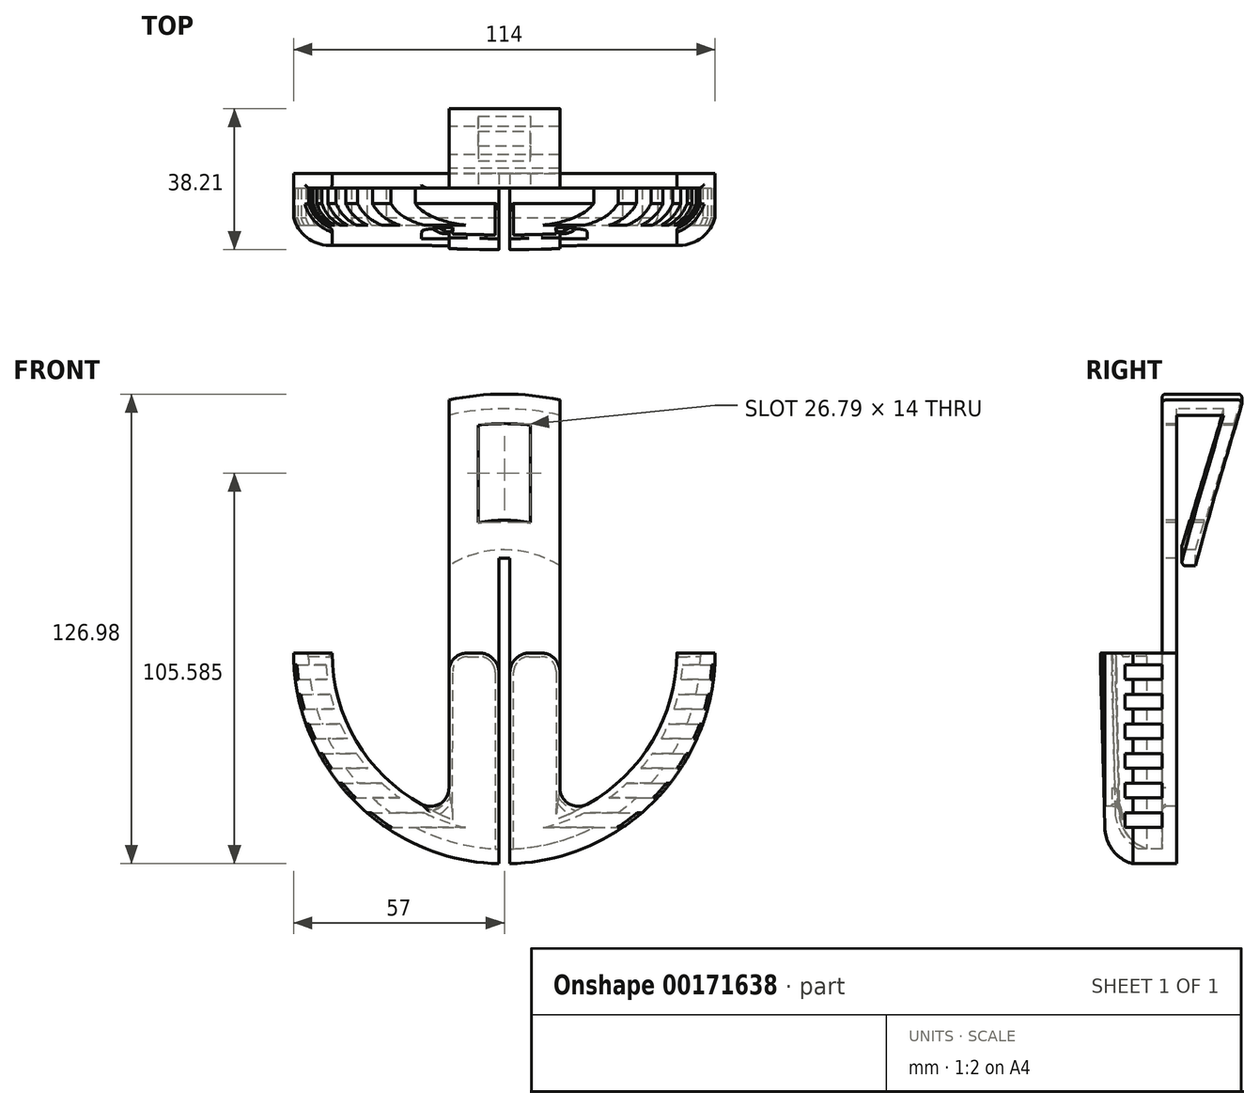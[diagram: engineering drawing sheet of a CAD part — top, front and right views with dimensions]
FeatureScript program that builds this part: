
annotation { "Feature Type Name" : "Feature", "Feature Type Description" : "" }
export const myFeature = defineFeature(function(context is Context, id is Id, definition is map)
    precondition{}
    {
        {
            var Q0;
            Q0=qCreatedBy(makeId("Top.planeOp"),FACE);
            var sketch = newSketch(context, id + "F0", { "sketchPlane" : qUnion([Q0])});
            skLineSegment(sketch, "E0", {"start": v(0, 0) * mm, "end": v(53, 0) * mm});
            skLineSegment(sketch, "E1", {"start": v(53, 0) * mm, "end": v(53, -4.13) * mm});
            skArc(sketch, "E2", {"start": v(42.97, -11.58) * mm, "mid": v(49.16, -9.44) * mm, "end": v(53, -4.13) * mm});
            skLineSegment(sketch, "E3", {"start": v(57, 4) * mm, "end": v(57, -7.88) * mm});
            skArc(sketch, "E4", {"start": v(47.4, -15.46) * mm, "mid": v(53.45, -13.27) * mm, "end": v(57, -7.88) * mm});
            skLineSegment(sketch, "E5", {"start": v(42.97, -11.58) * mm, "end": v(3.35, -12.64) * mm});
            skLineSegment(sketch, "E6", {"start": v(3.35, -12.64) * mm, "end": v(3.35, -16.64) * mm});
            skLineSegment(sketch, "E7", {"start": v(3.35, -16.64) * mm, "end": v(47.4, -15.46) * mm});
            skLineSegment(sketch, "E8", {"start": v(0, 4) * mm, "end": v(57, 4) * mm});
            skLineSegment(sketch, "E9", {"start": v(0, 4) * mm, "end": v(0, 0) * mm});
            skSolve(sketch);
        }
        {
            var Q0;
            Q0=makeQuery(id+"F0.imprint","IMPRINT",FACE,{"disambiguationData":[TD([[makeQuery(id+"F0.imprint","IMPRINT",EDGE,{"derivedFrom":sQuery(id+"F0.wireOp",EDGE,"E0")}),1.0]])]});
            var Q1;
            Q1=sQuery(id+"F0.wireOp",EDGE,"gh6nvR1q-v7TM-2IOc-XlZp-swlE0I2HpCQy");
            var Q2;
            Q2=sQuery(id+"F0.wireOp",EDGE,"O8IQiqjr-gjum-d30m-pnRi-cYj8KfRXyHnp");
            var Q3;
            Q3=sQuery(id+"F0.wireOp",EDGE,"gTedTpXi-uLA1-ukL2-yQAW-aUygu7Kv1SXh");
            var Q4;
            Q4=sQuery(id+"F0.wireOp",EDGE,"ZykMHYlj-tlNZ-H5aW-ebbf-Yw6o6fal1dPa");
            var Q5;
            Q5=sQuery(id+"F0.wireOp",EDGE,"cCRbS5nW-RNkD-MFLE-ALEK-Vklt7AKWVduu");
            var Q6;
            Q6=sQuery(id+"F0.wireOp",EDGE,"nLixHNUd-pwQR-5I1a-BRTQ-ecuvHCXoE5qB");
            var Q7;
            Q7=sQuery(id+"F0.wireOp",EDGE,"kgJvfNm7-WcT3-KGPc-acBb-M34wcv6vBjd2");
            var Q8;
            Q8=sQuery(id+"F0.wireOp",EDGE,"E5");
            var Q9;
            Q9=sQuery(id+"F0.wireOp",EDGE,"E2");
            var Q10;
            Q10=sQuery(id+"F0.wireOp",EDGE,"E4");
            var Q11;
            Q11=sQuery(id+"F0.wireOp",EDGE,"E7");
            var Q12;
            Q12=sQuery(id+"F0.wireOp",EDGE,"E3");
            var Q13;
            Q13=sQuery(id+"F0.wireOp",EDGE,"E1");
            var Q14;
            Q14=sQuery(id+"F0.wireOp",EDGE,"E6");
            var Q15;
            Q15=sQuery(id+"F0.wireOp",EDGE,"E9");
            revolve(context, id + "F1", {"entities" : qUnion([Q0]), "surfaceEntities" : qUnion([Q1, Q2, Q3, Q4, Q5, Q6, Q7, Q8, Q9, Q10, Q11, Q12, Q13, Q14]), "axis" : qUnion([Q15]), "revolveType" : RevolveType.ONE_DIRECTION, "oppositeDirection" : true, "angle" : 180 * degree});
        }
        {
            var Q0;
            Q0=qCreatedBy(makeId("Top.planeOp"),FACE);
            var sketch = newSketch(context, id + "F2", { "sketchPlane" : qUnion([Q0])});
            skLineSegment(sketch, "E10", {"start": v(0, 0) * mm, "end": v(-70, 0) * mm});
            skLineSegment(sketch, "E11", {"start": v(-70, 0) * mm, "end": v(-70, 21.93) * mm});
            skLineSegment(sketch, "E12", {"start": v(-70, 21.93) * mm, "end": v(-27.9, 9.03) * mm});
            skLineSegment(sketch, "E13", {"start": v(-27.9, 9.03) * mm, "end": v(-27.9, 5.03) * mm});
            skLineSegment(sketch, "E14", {"start": v(-27.9, 5.03) * mm, "end": v(-66, 16.7) * mm});
            skLineSegment(sketch, "E15", {"start": v(-66, 16.7) * mm, "end": v(-66, 4) * mm});
            skLineSegment(sketch, "E16", {"start": v(-66, 4) * mm, "end": v(0, 4) * mm});
            skLineSegment(sketch, "E17", {"start": v(0, 4) * mm, "end": v(0, 0) * mm});
            skSolve(sketch);
        }
        {
            var Q0;
            Q0=makeQuery(id+"F2.imprint","IMPRINT",FACE,{"disambiguationData":[TD([[makeQuery(id+"F2.imprint","IMPRINT",EDGE,{"derivedFrom":sQuery(id+"F2.wireOp",EDGE,"E10")}),-1.0]])]});
            var Q1;
            Q1=sQuery(id+"F2.wireOp",EDGE,"E17");
            revolve(context, id + "F3", {"operationType" : NewBodyOperationType.ADD, "entities" : qUnion([Q0]), "axis" : qUnion([Q1]), "revolveType" : RevolveType.ONE_DIRECTION, "oppositeDirection" : true, "angle" : 180 * degree});
        }
        {
            var Q0;
            Q0=qCreatedBy(makeId("Front.planeOp"),FACE);
            var sketch = newSketch(context, id + "F4", { "sketchPlane" : qUnion([Q0])});
            skLineSegment(sketch, "E18", {"start": v(-15, 0) * mm, "end": v(-15, 77.6) * mm});
            skLineSegment(sketch, "E19", {"start": v(-15, 77.6) * mm, "end": v(-78.11, 77.6) * mm});
            skLineSegment(sketch, "E20", {"start": v(-78.11, 77.6) * mm, "end": v(-78.11, 0) * mm});
            skLineSegment(sketch, "E21", {"start": v(-78.11, 0) * mm, "end": v(-46.6, 0) * mm});
            skLineSegment(sketch, "E22", {"start": v(-15, 0) * mm, "end": v(-15, -44.13) * mm});
            skArc(sketch, "E23", {"start": v(-46.6, 0) * mm, "mid": v(-37.89, -27.14) * mm, "end": v(-15, -44.13) * mm});
            skLineSegment(sketch, "E24.MirrorCS", {"start": v(15, 0) * mm, "end": v(15, 77.6) * mm});
            skLineSegment(sketch, "E25.MirrorCS", {"start": v(15, 77.6) * mm, "end": v(78.11, 77.6) * mm});
            skLineSegment(sketch, "E26.MirrorCS", {"start": v(78.11, 77.6) * mm, "end": v(78.11, 0) * mm});
            skLineSegment(sketch, "E27.MirrorCS", {"start": v(78.11, 0) * mm, "end": v(46.6, 0) * mm});
            skArc(sketch, "E28.MirrorCS", {"start": v(46.6, 0) * mm, "mid": v(37.89, -27.14) * mm, "end": v(15, -44.13) * mm});
            skLineSegment(sketch, "E29.MirrorCS", {"start": v(15, 0) * mm, "end": v(15, -44.13) * mm});
            skLineSegment(sketch, "E30", {"start": v(0, 25.58) * mm, "end": v(1.5, 25.58) * mm});
            skLineSegment(sketch, "E31", {"start": v(1.5, 25.58) * mm, "end": v(1.5, -61.51) * mm});
            skLineSegment(sketch, "E32", {"start": v(1.5, -61.51) * mm, "end": v(-1.5, -61.51) * mm});
            skLineSegment(sketch, "E33", {"start": v(-1.5, -61.51) * mm, "end": v(-1.5, 25.58) * mm});
            skLineSegment(sketch, "E34", {"start": v(-1.5, 25.58) * mm, "end": v(0, 25.58) * mm});
            skArc(sketch, "E35", {"start": v(7, 35.21) * mm, "mid": v(0, 35.9) * mm, "end": v(-7, 35.21) * mm});
            skLineSegment(sketch, "E36", {"start": v(7, 35.21) * mm, "end": v(7, 61.6) * mm});
            skLineSegment(sketch, "E37", {"start": v(-7, 61.6) * mm, "end": v(-7, 35.21) * mm});
            skArc(sketch, "E38", {"start": v(7, 61.6) * mm, "mid": v(0, 62) * mm, "end": v(-7, 61.6) * mm});
            skSolve(sketch);
        }
        {
            var Q0;
            Q0 = qSketchRegion(id + "F4", true);
            extrude(context, id + "F5", {"entities" : qUnion([Q0]), "operationType" : NewBodyOperationType.REMOVE, "oppositeDirection" : true, "depth" : 25 * mm, "hasSecondDirection" : true, "secondDirectionOppositeDirection" : false, "secondDirectionDepth" : 49.3 * mm});
        }
        {
            var Q0;
            Q0=makeQuery(id+"F5.boolean.opBoolean","INTERSECT",EDGE,{"derivedFrom":[makeQuery(id+"F3.boolean.opBoolean","MERGE",FACE,{"derivedFrom":[makeQuery(id+"F1.opRevolve","SWEPT_FACE",FACE,{"disambiguationData":[OSD([sQuery(id+"F0.wireOp",EDGE,"E0")])]}),makeQuery(id+"F3.opRevolve","SWEPT_FACE",FACE,{"disambiguationData":[OSD([sQuery(id+"F2.wireOp",EDGE,"E10")])]})]}),makeQuery(id+"F5.opExtrude","SWEPT_FACE",FACE,{"disambiguationData":[OSD([sQuery(id+"F4.wireOp",EDGE,"E23")])]})]});
            var Q1;
            Q1=makeQuery(id+"F5.boolean.opBoolean","INTERSECT",EDGE,{"derivedFrom":[makeQuery(id+"F3.boolean.opBoolean","MERGE",FACE,{"derivedFrom":[makeQuery(id+"F1.opRevolve","SWEPT_FACE",FACE,{"disambiguationData":[OSD([sQuery(id+"F0.wireOp",EDGE,"E0")])]}),makeQuery(id+"F3.opRevolve","SWEPT_FACE",FACE,{"disambiguationData":[OSD([sQuery(id+"F2.wireOp",EDGE,"E10")])]})]}),makeQuery(id+"F5.opExtrude","SWEPT_FACE",FACE,{"disambiguationData":[OSD([sQuery(id+"F4.wireOp",EDGE,"E21")])]})]});
            var Q2;
            Q2=makeQuery(id+"F1.opRevolve","CAP_EDGE",EDGE,{"disambiguationData":[OSD([sQuery(id+"F0.wireOp",EDGE,"E1")])],"isStart":false});
            var Q3;
            Q3=makeQuery(id+"F1.opRevolve","CAP_EDGE",EDGE,{"disambiguationData":[OSD([sQuery(id+"F0.wireOp",EDGE,"E2")])],"isStart":false});
            var Q4;
            Q4=makeQuery(id+"F5.boolean.opBoolean","INTERSECT",EDGE,{"derivedFrom":[makeQuery(id+"F1.opRevolve","SWEPT_FACE",FACE,{"disambiguationData":[OSD([sQuery(id+"F0.wireOp",EDGE,"E2")])]}),makeQuery(id+"F5.opExtrude","SWEPT_FACE",FACE,{"disambiguationData":[OSD([sQuery(id+"F4.wireOp",EDGE,"E23")])]})]});
            var Q5;
            Q5=makeQuery(id+"F5.boolean.opBoolean","INTERSECT",EDGE,{"derivedFrom":[makeQuery(id+"F1.opRevolve","SWEPT_FACE",FACE,{"disambiguationData":[OSD([sQuery(id+"F0.wireOp",EDGE,"E2")])]}),makeQuery(id+"F5.opExtrude","SWEPT_FACE",FACE,{"disambiguationData":[OSD([sQuery(id+"F4.wireOp",EDGE,"E18"),sQuery(id+"F4.wireOp",EDGE,"E22")])]})]});
            var Q6;
            Q6=makeQuery(id+"F5.boolean.opBoolean","INTERSECT",EDGE,{"derivedFrom":[makeQuery(id+"F1.opRevolve","SWEPT_FACE",FACE,{"disambiguationData":[OSD([sQuery(id+"F0.wireOp",EDGE,"E5")])]}),makeQuery(id+"F5.opExtrude","SWEPT_FACE",FACE,{"disambiguationData":[OSD([sQuery(id+"F4.wireOp",EDGE,"E18"),sQuery(id+"F4.wireOp",EDGE,"E22")])]})]});
            var Q7;
            Q7=makeQuery(id+"F1.opRevolve","CAP_EDGE",EDGE,{"disambiguationData":[OSD([sQuery(id+"F0.wireOp",EDGE,"E5")])],"isStart":false});
            var Q8;
            {var subQ0=sQuery(id+"F0.wireOp",EDGE,"E6");var subQ1=sQuery(id+"F0.wireOp",EDGE,"E5");Q8=makeQuery(id+"F5.boolean.opBoolean","SPLIT",EDGE,{"disambiguationData":[TD([makeQuery(id+"F5.opExtrude","SWEPT_FACE",FACE,{"disambiguationData":[OSD([sQuery(id+"F4.wireOp",EDGE,"E33")])]})])],"derivedFrom":makeQuery(id+"F1.opRevolve","SWEPT_EDGE",EDGE,{"disambiguationData":[OSD([subQ1,subQ0])]})});}
            var Q9;
            Q9=makeQuery(id+"F5.boolean.opBoolean","INTERSECT",EDGE,{"derivedFrom":[makeQuery(id+"F1.opRevolve","SWEPT_FACE",FACE,{"disambiguationData":[OSD([sQuery(id+"F0.wireOp",EDGE,"E5")])]}),makeQuery(id+"F5.opExtrude","SWEPT_FACE",FACE,{"disambiguationData":[OSD([sQuery(id+"F4.wireOp",EDGE,"E33")])]})]});
            var Q10;
            Q10=makeQuery(id+"F5.boolean.opBoolean","INTERSECT",EDGE,{"derivedFrom":[makeQuery(id+"F1.opRevolve","SWEPT_FACE",FACE,{"disambiguationData":[OSD([sQuery(id+"F0.wireOp",EDGE,"E2")])]}),makeQuery(id+"F5.opExtrude","SWEPT_FACE",FACE,{"disambiguationData":[OSD([sQuery(id+"F4.wireOp",EDGE,"E31")])]})]});
            var Q11;
            {var subQ0=sQuery(id+"F0.wireOp",EDGE,"E6");var subQ1=sQuery(id+"F0.wireOp",EDGE,"E5");Q11=makeQuery(id+"F5.boolean.opBoolean","SPLIT",EDGE,{"disambiguationData":[TD([makeQuery(id+"F5.opExtrude","SWEPT_FACE",FACE,{"disambiguationData":[OSD([sQuery(id+"F4.wireOp",EDGE,"E31")])]})])],"derivedFrom":makeQuery(id+"F1.opRevolve","SWEPT_EDGE",EDGE,{"disambiguationData":[OSD([subQ1,subQ0])]})});}
            var Q12;
            Q12=makeQuery(id+"F1.opRevolve","CAP_EDGE",EDGE,{"disambiguationData":[OSD([sQuery(id+"F0.wireOp",EDGE,"E5")])],"isStart":true});
            var Q13;
            Q13=makeQuery(id+"F5.boolean.opBoolean","INTERSECT",EDGE,{"derivedFrom":[makeQuery(id+"F1.opRevolve","SWEPT_FACE",FACE,{"disambiguationData":[OSD([sQuery(id+"F0.wireOp",EDGE,"E5")])]}),makeQuery(id+"F5.opExtrude","SWEPT_FACE",FACE,{"disambiguationData":[OSD([sQuery(id+"F4.wireOp",EDGE,"E24.MirrorCS"),sQuery(id+"F4.wireOp",EDGE,"E29.MirrorCS")])]})]});
            var Q14;
            Q14=makeQuery(id+"F5.boolean.opBoolean","INTERSECT",EDGE,{"derivedFrom":[makeQuery(id+"F1.opRevolve","SWEPT_FACE",FACE,{"disambiguationData":[OSD([sQuery(id+"F0.wireOp",EDGE,"E2")])]}),makeQuery(id+"F5.opExtrude","SWEPT_FACE",FACE,{"disambiguationData":[OSD([sQuery(id+"F4.wireOp",EDGE,"E28.MirrorCS")])]})]});
            var Q15;
            Q15=makeQuery(id+"F1.opRevolve","CAP_EDGE",EDGE,{"disambiguationData":[OSD([sQuery(id+"F0.wireOp",EDGE,"E2")])],"isStart":true});
            var Q16;
            Q16=makeQuery(id+"F5.boolean.opBoolean","INTERSECT",EDGE,{"derivedFrom":[makeQuery(id+"F3.boolean.opBoolean","MERGE",FACE,{"derivedFrom":[makeQuery(id+"F1.opRevolve","SWEPT_FACE",FACE,{"disambiguationData":[OSD([sQuery(id+"F0.wireOp",EDGE,"E0")])]}),makeQuery(id+"F3.opRevolve","SWEPT_FACE",FACE,{"disambiguationData":[OSD([sQuery(id+"F2.wireOp",EDGE,"E10")])]})]}),makeQuery(id+"F5.opExtrude","SWEPT_FACE",FACE,{"disambiguationData":[OSD([sQuery(id+"F4.wireOp",EDGE,"E27.MirrorCS")])]})]});
            var Q17;
            Q17=makeQuery(id+"F1.opRevolve","CAP_EDGE",EDGE,{"disambiguationData":[OSD([sQuery(id+"F0.wireOp",EDGE,"E1")])],"isStart":true});
            var Q18;
            Q18=makeQuery(id+"F3.opRevolve","SWEPT_EDGE",EDGE,{"disambiguationData":[OSD([sQuery(id+"F2.wireOp",EDGE,"E10"),sQuery(id+"F2.wireOp",EDGE,"E11")])]});
            var Q19;
            Q19=makeQuery(id+"F3.opRevolve","SWEPT_EDGE",EDGE,{"disambiguationData":[OSD([sQuery(id+"F2.wireOp",EDGE,"E11"),sQuery(id+"F2.wireOp",EDGE,"E12")])]});
            var Q20;
            Q20=makeQuery(id+"F3.opRevolve","SWEPT_EDGE",EDGE,{"disambiguationData":[OSD([sQuery(id+"F2.wireOp",EDGE,"E13"),sQuery(id+"F2.wireOp",EDGE,"E14")])]});
            fillet(context, id + "F6", {"entities" : qUnion([Q0, Q1, Q2, Q3, Q4, Q5, Q6, Q7, Q8, Q9, Q10, Q11, Q12, Q13, Q14, Q15, Q16, Q17, Q18, Q19, Q20]), "radius" : 1 * mm, "tangentPropagation" : true, "allowEdgeOverflow" : false});
        }
        {
            var Q0;
            Q0=qCreatedBy(makeId("Right.planeOp"),FACE);
            var sketch = newSketch(context, id + "F7", { "sketchPlane" : qUnion([Q0])});
            skLineSegment(sketch, "E39.bottom", {"start": v(0, -3.18) * mm, "end": v(-10, -3.18) * mm});
            skLineSegment(sketch, "E39.top", {"start": v(0, -7.18) * mm, "end": v(-10, -7.18) * mm});
            skLineSegment(sketch, "E39.left", {"start": v(0, -3.18) * mm, "end": v(0, -7.18) * mm});
            skLineSegment(sketch, "E39.right", {"start": v(-10, -3.18) * mm, "end": v(-10, -7.18) * mm});
            skLineSegment(sketch, "E40.0.1.0", {"start": v(0, -15.18) * mm, "end": v(-10, -15.18) * mm});
            skLineSegment(sketch, "E40.0.1.1", {"start": v(0, -11.18) * mm, "end": v(-10, -11.18) * mm});
            skLineSegment(sketch, "E40.0.1.2", {"start": v(-10, -11.18) * mm, "end": v(-10, -15.18) * mm});
            skLineSegment(sketch, "E40.0.1.3", {"start": v(0, -11.18) * mm, "end": v(0, -15.18) * mm});
            skLineSegment(sketch, "E40.0.2.0", {"start": v(0, -23.18) * mm, "end": v(-10, -23.18) * mm});
            skLineSegment(sketch, "E40.0.2.1", {"start": v(0, -19.18) * mm, "end": v(-10, -19.18) * mm});
            skLineSegment(sketch, "E40.0.2.2", {"start": v(-10, -19.18) * mm, "end": v(-10, -23.18) * mm});
            skLineSegment(sketch, "E40.0.2.3", {"start": v(0, -19.18) * mm, "end": v(0, -23.18) * mm});
            skLineSegment(sketch, "E40.0.3.0", {"start": v(0, -31.18) * mm, "end": v(-10, -31.18) * mm});
            skLineSegment(sketch, "E40.0.3.1", {"start": v(0, -27.18) * mm, "end": v(-10, -27.18) * mm});
            skLineSegment(sketch, "E40.0.3.2", {"start": v(-10, -27.18) * mm, "end": v(-10, -31.18) * mm});
            skLineSegment(sketch, "E40.0.3.3", {"start": v(0, -27.18) * mm, "end": v(0, -31.18) * mm});
            skLineSegment(sketch, "E40.0.4.0", {"start": v(0, -39.18) * mm, "end": v(-10, -39.18) * mm});
            skLineSegment(sketch, "E40.0.4.1", {"start": v(0, -35.18) * mm, "end": v(-10, -35.18) * mm});
            skLineSegment(sketch, "E40.0.4.2", {"start": v(-10, -35.18) * mm, "end": v(-10, -39.18) * mm});
            skLineSegment(sketch, "E40.0.4.3", {"start": v(0, -35.18) * mm, "end": v(0, -39.18) * mm});
            skLineSegment(sketch, "E40.0.5.0", {"start": v(0, -47.18) * mm, "end": v(-10, -47.18) * mm});
            skLineSegment(sketch, "E40.0.5.1", {"start": v(0, -43.18) * mm, "end": v(-10, -43.18) * mm});
            skLineSegment(sketch, "E40.0.5.2", {"start": v(-10, -43.18) * mm, "end": v(-10, -47.18) * mm});
            skLineSegment(sketch, "E40.0.5.3", {"start": v(0, -43.18) * mm, "end": v(0, -47.18) * mm});
            skLineSegment(sketch, "E40.direction1", {"start": v(-10, -7.18) * mm, "end": v(15, -7.18) * mm, "construction": true});
            skLineSegment(sketch, "E40.direction2", {"start": v(-10, -7.18) * mm, "end": v(-10, -15.18) * mm, "construction": true});
            skSolve(sketch);
        }
        {
            var Q0;
            Q0 = qSketchRegion(id + "F7", true);
            extrude(context, id + "F8", {"entities" : qUnion([Q0]), "operationType" : NewBodyOperationType.REMOVE, "oppositeDirection" : true, "depth" : 60 * mm, "hasSecondDirection" : true, "secondDirectionOppositeDirection" : false, "secondDirectionDepth" : 60 * mm});
        }
        {
            var Q0;
            Q0=makeQuery(id+"F5.boolean.opBoolean","INTERSECT",EDGE,{"derivedFrom":[makeQuery(id+"F3.boolean.opBoolean","SPLIT",FACE,{"disambiguationData":[OD(1.0)],"derivedFrom":makeQuery(id+"F1.opRevolve","CAP_FACE",FACE,{"disambiguationData":[OSD([sQuery(id+"F0.wireOp",EDGE,"E0"),sQuery(id+"F0.wireOp",EDGE,"E1"),sQuery(id+"F0.wireOp",EDGE,"E2"),sQuery(id+"F0.wireOp",EDGE,"E3"),sQuery(id+"F0.wireOp",EDGE,"E4"),sQuery(id+"F0.wireOp",EDGE,"E5"),sQuery(id+"F0.wireOp",EDGE,"E6"),sQuery(id+"F0.wireOp",EDGE,"E7"),sQuery(id+"F0.wireOp",EDGE,"E8"),sQuery(id+"F0.wireOp",EDGE,"E9")])],"isStart":false})}),makeQuery(id+"F5.opExtrude","SWEPT_FACE",FACE,{"disambiguationData":[OSD([sQuery(id+"F4.wireOp",EDGE,"E18"),sQuery(id+"F4.wireOp",EDGE,"E22")])]})]});
            var Q1;
            Q1=makeQuery(id+"F5.boolean.opBoolean","INTERSECT",EDGE,{"derivedFrom":[makeQuery(id+"F3.boolean.opBoolean","SPLIT",FACE,{"disambiguationData":[OD(0.0)],"derivedFrom":makeQuery(id+"F1.opRevolve","CAP_FACE",FACE,{"disambiguationData":[OSD([sQuery(id+"F0.wireOp",EDGE,"E0"),sQuery(id+"F0.wireOp",EDGE,"E1"),sQuery(id+"F0.wireOp",EDGE,"E2"),sQuery(id+"F0.wireOp",EDGE,"E3"),sQuery(id+"F0.wireOp",EDGE,"E4"),sQuery(id+"F0.wireOp",EDGE,"E5"),sQuery(id+"F0.wireOp",EDGE,"E6"),sQuery(id+"F0.wireOp",EDGE,"E7"),sQuery(id+"F0.wireOp",EDGE,"E8"),sQuery(id+"F0.wireOp",EDGE,"E9")])],"isStart":false})}),makeQuery(id+"F5.opExtrude","SWEPT_FACE",FACE,{"disambiguationData":[OSD([sQuery(id+"F4.wireOp",EDGE,"E24.MirrorCS"),sQuery(id+"F4.wireOp",EDGE,"E29.MirrorCS")])]}),makeQuery(id+"F5.opExtrude","SWEPT_FACE",FACE,{"disambiguationData":[OSD([sQuery(id+"F4.wireOp",EDGE,"E27.MirrorCS")])]})]});
            var Q2;
            {var subQ0=sQuery(id+"F4.wireOp",EDGE,"E23");var subQ1=sQuery(id+"F4.wireOp",EDGE,"E22");Q2=makeQuery(id+"F5.boolean.opBoolean","COPY",EDGE,{"disambiguationData":[TD([makeQuery(id+"F1.opRevolve","SWEPT_FACE",FACE,{"disambiguationData":[OSD([sQuery(id+"F0.wireOp",EDGE,"E0")])]})])],"derivedFrom":makeQuery(id+"F5.opExtrude","SWEPT_EDGE",EDGE,{"disambiguationData":[OSD([subQ1,subQ0])]})});}
            var Q3;
            {var subQ0=sQuery(id+"F4.wireOp",EDGE,"E22");var subQ1=sQuery(id+"F4.wireOp",EDGE,"E23");Q3=makeQuery(id+"F5.boolean.opBoolean","COPY",EDGE,{"disambiguationData":[TD([makeQuery(id+"F1.opRevolve","SWEPT_FACE",FACE,{"disambiguationData":[OSD([sQuery(id+"F0.wireOp",EDGE,"E2")])]})])],"derivedFrom":makeQuery(id+"F5.opExtrude","SWEPT_EDGE",EDGE,{"disambiguationData":[OSD([subQ0,subQ1])]})});}
            var Q4;
            {var subQ0=sQuery(id+"F4.wireOp",EDGE,"E29.MirrorCS");var subQ1=sQuery(id+"F4.wireOp",EDGE,"E28.MirrorCS");Q4=makeQuery(id+"F5.boolean.opBoolean","COPY",EDGE,{"disambiguationData":[TD([makeQuery(id+"F1.opRevolve","SWEPT_FACE",FACE,{"disambiguationData":[OSD([sQuery(id+"F0.wireOp",EDGE,"E0")])]})])],"derivedFrom":makeQuery(id+"F5.opExtrude","SWEPT_EDGE",EDGE,{"disambiguationData":[OSD([subQ1,subQ0])]})});}
            var Q5;
            {var subQ0=sQuery(id+"F4.wireOp",EDGE,"E29.MirrorCS");var subQ1=sQuery(id+"F4.wireOp",EDGE,"E28.MirrorCS");Q5=makeQuery(id+"F5.boolean.opBoolean","COPY",EDGE,{"disambiguationData":[TD([makeQuery(id+"F1.opRevolve","SWEPT_FACE",FACE,{"disambiguationData":[OSD([sQuery(id+"F0.wireOp",EDGE,"E2")])]})])],"derivedFrom":makeQuery(id+"F5.opExtrude","SWEPT_EDGE",EDGE,{"disambiguationData":[OSD([subQ1,subQ0])]})});}
            var Q6;
            Q6=makeQuery(id+"F1.opRevolve","CAP_EDGE",EDGE,{"disambiguationData":[OSD([sQuery(id+"F0.wireOp",EDGE,"E6")])],"isStart":false});
            var Q7;
            Q7=makeQuery(id+"F1.opRevolve","CAP_EDGE",EDGE,{"disambiguationData":[OSD([sQuery(id+"F0.wireOp",EDGE,"E6")])],"isStart":true});
            var Q8;
            Q8=makeQuery(id+"F5.boolean.opBoolean","INTERSECT",EDGE,{"derivedFrom":[makeQuery(id+"F1.opRevolve","SWEPT_FACE",FACE,{"disambiguationData":[OSD([sQuery(id+"F0.wireOp",EDGE,"E6")])]}),makeQuery(id+"F5.opExtrude","SWEPT_FACE",FACE,{"disambiguationData":[OSD([sQuery(id+"F4.wireOp",EDGE,"E31")])]})]});
            var Q9;
            Q9=makeQuery(id+"F5.boolean.opBoolean","INTERSECT",EDGE,{"derivedFrom":[makeQuery(id+"F1.opRevolve","SWEPT_FACE",FACE,{"disambiguationData":[OSD([sQuery(id+"F0.wireOp",EDGE,"E6")])]}),makeQuery(id+"F5.opExtrude","SWEPT_FACE",FACE,{"disambiguationData":[OSD([sQuery(id+"F4.wireOp",EDGE,"E33")])]})]});
            fillet(context, id + "F9", {"entities" : qUnion([Q0, Q1, Q2, Q3, Q4, Q5, Q6, Q7, Q8, Q9]), "radius" : 5 * mm, "tangentPropagation" : true, "allowEdgeOverflow" : false});
        }
    });
